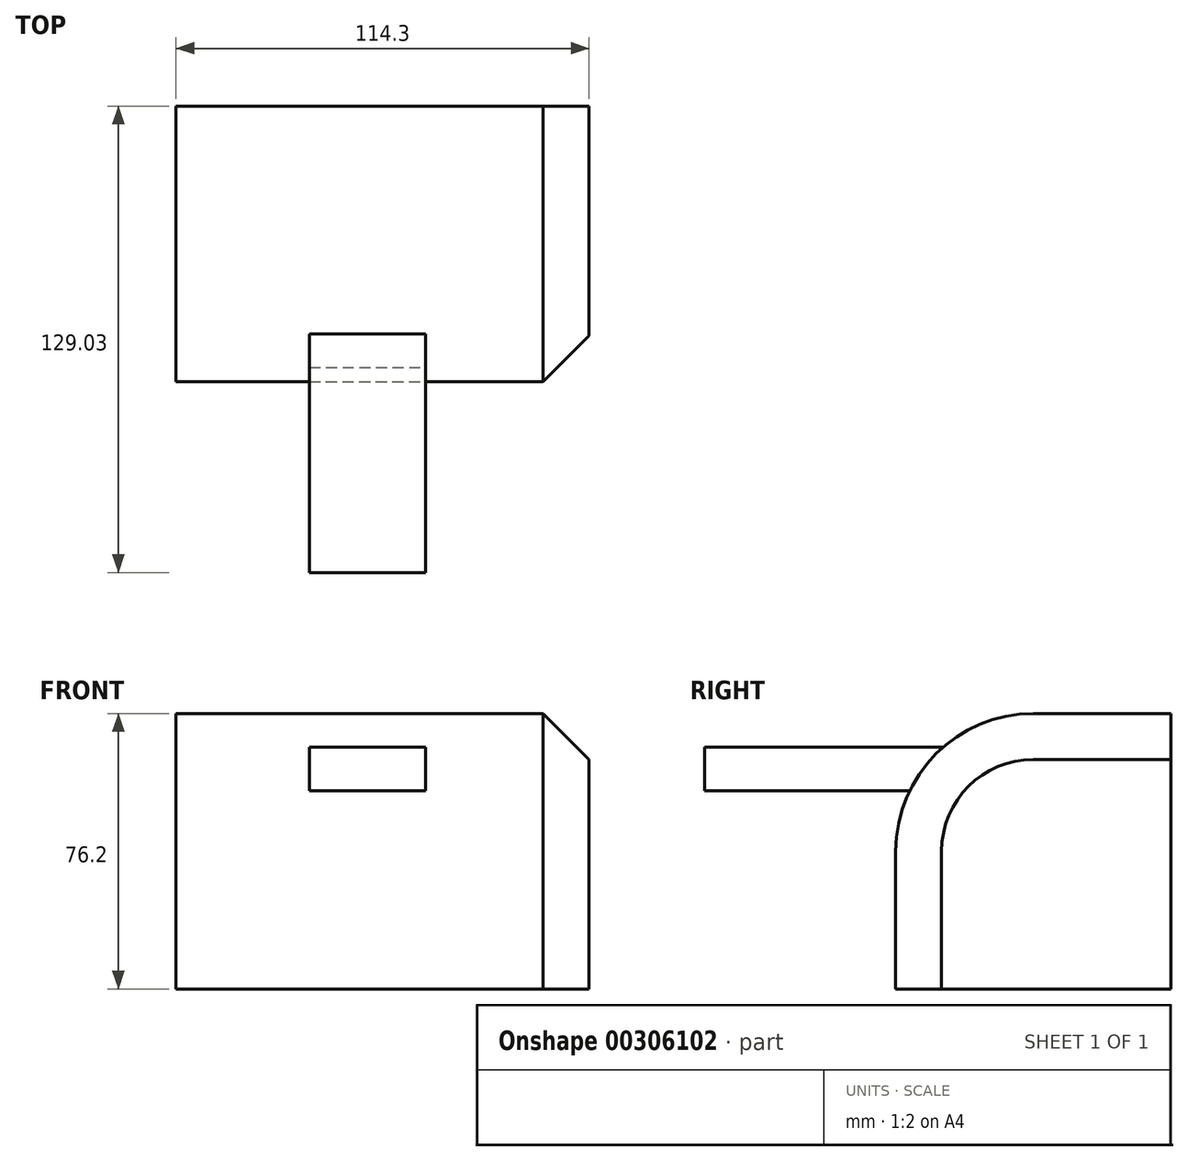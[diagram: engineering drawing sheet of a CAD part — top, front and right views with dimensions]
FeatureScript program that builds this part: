
annotation { "Feature Type Name" : "Feature", "Feature Type Description" : "" }
export const myFeature = defineFeature(function(context is Context, id is Id, definition is map)
    precondition{}
    {
        {
            var Q0;
            Q0=qCreatedBy(makeId("Front.planeOp"),FACE);
            var sketch = newSketch(context, id + "F0", { "sketchPlane" : qUnion([Q0])});
            skLineSegment(sketch, "E0.bottom", {"start": v(-57.55, 32.03) * mm, "end": v(56.75, 32.03) * mm});
            skLineSegment(sketch, "E0.top", {"start": v(-57.55, -44.17) * mm, "end": v(56.75, -44.17) * mm});
            skLineSegment(sketch, "E0.left", {"start": v(-57.55, 32.03) * mm, "end": v(-57.55, -44.17) * mm});
            skLineSegment(sketch, "E0.right", {"start": v(56.75, 32.03) * mm, "end": v(56.75, -44.17) * mm});
            skSolve(sketch);
        }
        {
            var Q0;
            Q0 = qSketchRegion(id + "F0", true);
            extrude(context, id + "F1", {"entities" : qUnion([Q0]), "endBound" : BoundingType.SYMMETRIC, "depth" : 76.2 * mm});
        }
        {
            var Q0;
            Q0=makeQuery(id+"F1.opExtrude","CAP_EDGE",EDGE,{"disambiguationData":[OSD([sQuery(id+"F0.wireOp",EDGE,"E0.bottom")])],"isStart":false});
            fillet(context, id + "F2", {"entities" : qUnion([Q0]), "radius" : 38.1 * mm, "tangentPropagation" : true, "allowEdgeOverflow" : false});
        }
        {
            var Q0;
            Q0=makeQuery(id+"F1.opExtrude","SWEPT_EDGE",EDGE,{"disambiguationData":[OSD([sQuery(id+"F0.wireOp",EDGE,"E0.bottom"),sQuery(id+"F0.wireOp",EDGE,"E0.right")])]});
            chamfer(context, id + "F3", {"entities" : qUnion([Q0]), "width" : 12.7 * mm, "tangentPropagation" : true});
        }
        {
            var Q0;
            Q0=qCreatedBy(makeId("Front.planeOp"),FACE);
            var sketch = newSketch(context, id + "F4", { "sketchPlane" : qUnion([Q0])});
            skLineSegment(sketch, "E1.bottom", {"start": v(-20.62, 22.75) * mm, "end": v(11.48, 22.75) * mm});
            skLineSegment(sketch, "E1.top", {"start": v(-20.62, 10.7) * mm, "end": v(11.48, 10.7) * mm});
            skLineSegment(sketch, "E1.left", {"start": v(-20.62, 22.75) * mm, "end": v(-20.62, 10.7) * mm});
            skLineSegment(sketch, "E1.right", {"start": v(11.48, 22.75) * mm, "end": v(11.48, 10.7) * mm});
            skSolve(sketch);
        }
        {
            var Q0;
            Q0 = qSketchRegion(id + "F4", true);
            extrude(context, id + "F5", {"entities" : qUnion([Q0]), "operationType" : NewBodyOperationType.ADD, "depth" : 90.93 * mm});
        }
    });
